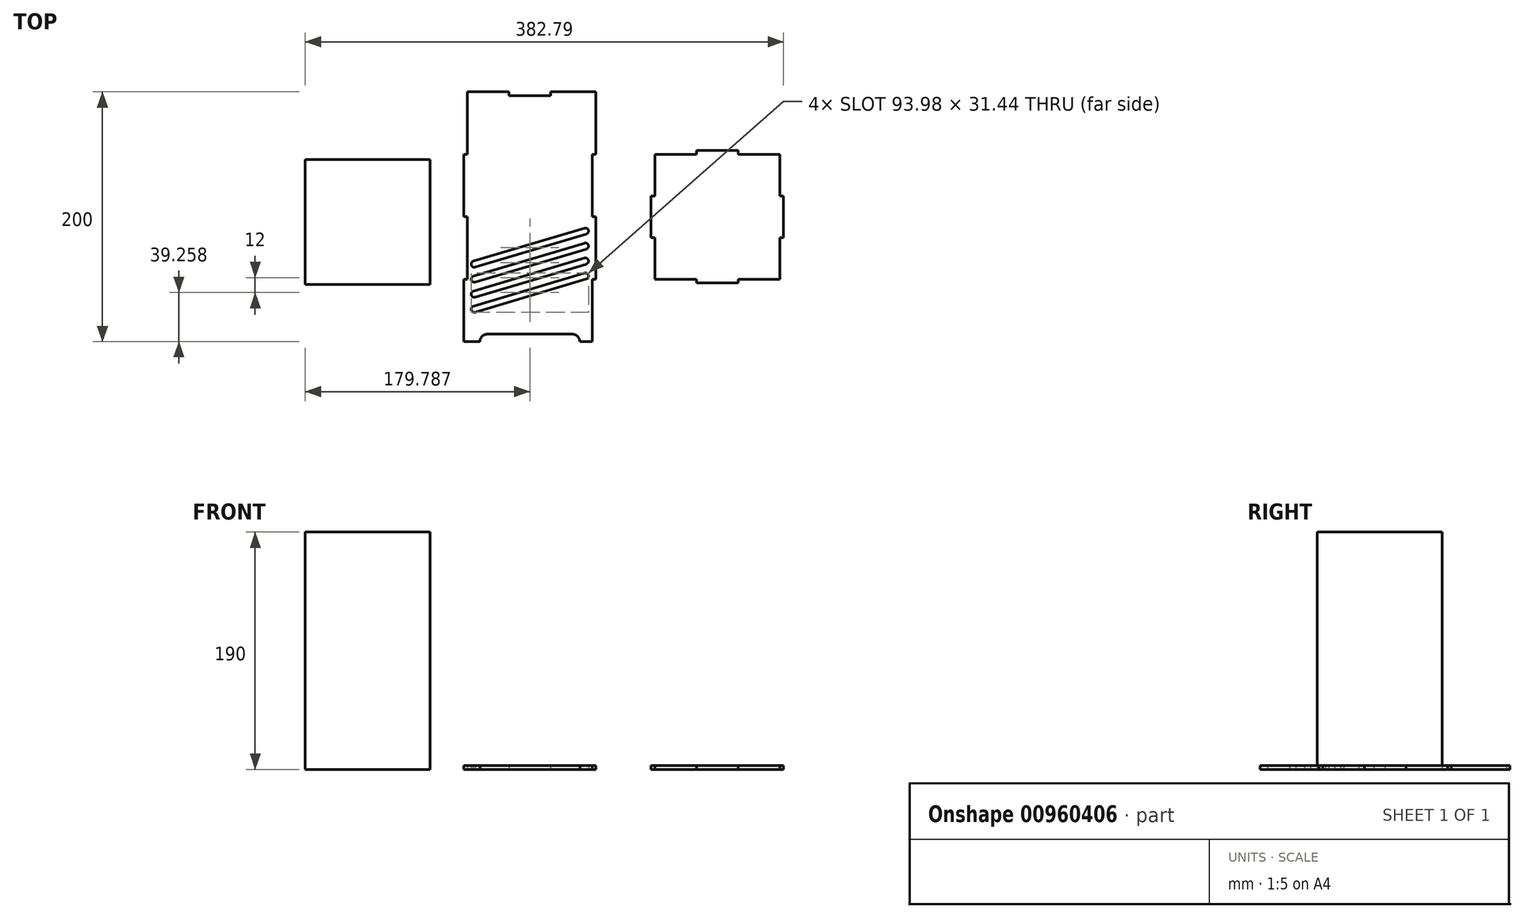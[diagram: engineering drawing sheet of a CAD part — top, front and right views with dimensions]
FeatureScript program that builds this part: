
annotation { "Feature Type Name" : "Feature", "Feature Type Description" : "" }
export const myFeature = defineFeature(function(context is Context, id is Id, definition is map)
    precondition{}
    {
        {
            var Q0;
            Q0=qCreatedBy(makeId("Top.planeOp"),FACE);
            var sketch = newSketch(context, id + "F0", { "sketchPlane" : qUnion([Q0])});
            skLineSegment(sketch, "E0.bottom", {"start": v(50, 100) * mm, "end": v(-50, 100) * mm, "construction": true});
            skLineSegment(sketch, "E0.top", {"start": v(50, -100) * mm, "end": v(-50, -100) * mm, "construction": true});
            skLineSegment(sketch, "E0.left", {"start": v(50, 100) * mm, "end": v(50, -100) * mm, "construction": true});
            skLineSegment(sketch, "E0.right", {"start": v(-50, 100) * mm, "end": v(-50, -100) * mm, "construction": true});
            skLineSegment(sketch, "E1", {"start": v(-50, 100) * mm, "end": v(-50, 50) * mm});
            skLineSegment(sketch, "E2", {"start": v(-50, 50) * mm, "end": v(-53, 50) * mm});
            skLineSegment(sketch, "E3", {"start": v(-53, 50) * mm, "end": v(-53, 0) * mm});
            skLineSegment(sketch, "E4", {"start": v(-53, 0) * mm, "end": v(-50, 0) * mm});
            skLineSegment(sketch, "E5", {"start": v(-50, 0) * mm, "end": v(-50, -50) * mm});
            skLineSegment(sketch, "E6", {"start": v(-50, -50) * mm, "end": v(-53, -50) * mm});
            skLineSegment(sketch, "E7", {"start": v(-53, -50) * mm, "end": v(-53, -100) * mm});
            skLineSegment(sketch, "E8", {"start": v(-53, -100) * mm, "end": v(-50, -100) * mm});
            skLineSegment(sketch, "E9", {"start": v(50, 100) * mm, "end": v(53, 100) * mm});
            skLineSegment(sketch, "E10", {"start": v(53, 100) * mm, "end": v(53, 50) * mm});
            skLineSegment(sketch, "E11", {"start": v(53, 50) * mm, "end": v(50, 50) * mm});
            skLineSegment(sketch, "E12", {"start": v(50, 50) * mm, "end": v(50, 0) * mm});
            skLineSegment(sketch, "E13", {"start": v(50, 0) * mm, "end": v(53, 0) * mm});
            skLineSegment(sketch, "E14", {"start": v(53, 0) * mm, "end": v(53, -50) * mm});
            skLineSegment(sketch, "E15", {"start": v(53, -50) * mm, "end": v(50, -50) * mm});
            skLineSegment(sketch, "E16", {"start": v(50, -50) * mm, "end": v(50, -100) * mm});
            skLineSegment(sketch, "E17", {"start": v(50, -100) * mm, "end": v(-50, -100) * mm});
            skLineSegment(sketch, "E18.bottom", {"start": v(100, -50) * mm, "end": v(200, -50) * mm, "construction": true});
            skLineSegment(sketch, "E18.top", {"start": v(100, 50) * mm, "end": v(200, 50) * mm, "construction": true});
            skLineSegment(sketch, "E18.left", {"start": v(100, -50) * mm, "end": v(100, 50) * mm, "construction": true});
            skLineSegment(sketch, "E18.right", {"start": v(200, -50) * mm, "end": v(200, 50) * mm, "construction": true});
            skPoint(sketch, "E18.middle", {"position": v(150, 0) * mm});
            skLineSegment(sketch, "E19", {"start": v(100, 50) * mm, "end": v(133.33, 50) * mm});
            skLineSegment(sketch, "E20", {"start": v(133.33, 50) * mm, "end": v(133.33, 53) * mm});
            skLineSegment(sketch, "E21", {"start": v(133.33, 53) * mm, "end": v(166.67, 53) * mm});
            skLineSegment(sketch, "E22", {"start": v(166.67, 53) * mm, "end": v(166.67, 50) * mm});
            skLineSegment(sketch, "E23", {"start": v(166.67, 50) * mm, "end": v(200, 50) * mm});
            skLineSegment(sketch, "E24", {"start": v(-50, 100) * mm, "end": v(-16.67, 100) * mm});
            skLineSegment(sketch, "E25", {"start": v(-16.67, 97) * mm, "end": v(-16.67, 100) * mm});
            skLineSegment(sketch, "E26", {"start": v(-16.67, 97) * mm, "end": v(16.67, 97) * mm});
            skLineSegment(sketch, "E27", {"start": v(16.67, 100) * mm, "end": v(16.67, 97) * mm});
            skLineSegment(sketch, "E28", {"start": v(16.67, 100) * mm, "end": v(50, 100) * mm});
            skLineSegment(sketch, "E29.1.1", {"start": v(97, -16.67) * mm, "end": v(97, 16.67) * mm});
            skLineSegment(sketch, "E29.1.2", {"start": v(100, -50) * mm, "end": v(100, -16.67) * mm});
            skLineSegment(sketch, "E29.1.3", {"start": v(100, 16.67) * mm, "end": v(100, 50) * mm});
            skLineSegment(sketch, "E29.1.4", {"start": v(100, -16.67) * mm, "end": v(97, -16.67) * mm});
            skLineSegment(sketch, "E29.1.5", {"start": v(97, 16.67) * mm, "end": v(100, 16.67) * mm});
            skLineSegment(sketch, "E29.2.0", {"start": v(200, -50) * mm, "end": v(100, -50) * mm, "construction": true});
            skLineSegment(sketch, "E29.2.1", {"start": v(166.67, -53) * mm, "end": v(133.33, -53) * mm});
            skLineSegment(sketch, "E29.2.2", {"start": v(200, -50) * mm, "end": v(166.67, -50) * mm});
            skLineSegment(sketch, "E29.2.3", {"start": v(133.33, -50) * mm, "end": v(100, -50) * mm});
            skLineSegment(sketch, "E29.2.4", {"start": v(166.67, -50) * mm, "end": v(166.67, -53) * mm});
            skLineSegment(sketch, "E29.2.5", {"start": v(133.33, -53) * mm, "end": v(133.33, -50) * mm});
            skLineSegment(sketch, "E29.3.0", {"start": v(200, 50) * mm, "end": v(200, -50) * mm, "construction": true});
            skLineSegment(sketch, "E29.3.1", {"start": v(203, 16.67) * mm, "end": v(203, -16.67) * mm});
            skLineSegment(sketch, "E29.3.2", {"start": v(200, 50) * mm, "end": v(200, 16.67) * mm});
            skLineSegment(sketch, "E29.3.3", {"start": v(200, -16.67) * mm, "end": v(200, -50) * mm});
            skLineSegment(sketch, "E29.3.4", {"start": v(200, 16.67) * mm, "end": v(203, 16.67) * mm});
            skLineSegment(sketch, "E29.3.5", {"start": v(203, -16.67) * mm, "end": v(200, -16.67) * mm});
            skLineSegment(sketch, "E30.bottom", {"start": v(-47, 94) * mm, "end": v(47, 94) * mm, "construction": true});
            skLineSegment(sketch, "E30.left", {"start": v(-47, 94) * mm, "end": v(-47, -90) * mm, "construction": true});
            skLineSegment(sketch, "E30.right", {"start": v(47, 94) * mm, "end": v(47, -90) * mm, "construction": true});
            skPoint(sketch, "E31", {"position": v(0, 94) * mm});
            skArc(sketch, "E32", {"start": v(40, -100) * mm, "mid": v(38.24, -95.76) * mm, "end": v(34, -94) * mm});
            skArc(sketch, "E33", {"start": v(-40, -100) * mm, "mid": v(-38.24, -95.76) * mm, "end": v(-34, -94) * mm});
            skLineSegment(sketch, "E34", {"start": v(-34, -94) * mm, "end": v(34, -94) * mm});
            skLineSegment(sketch, "E35", {"start": v(-47, -90) * mm, "end": v(47, -90) * mm, "construction": true});
            skLineSegment(sketch, "E36", {"start": v(-45.28, -71.6) * mm, "end": v(43.79, -45.11) * mm});
            skLineSegment(sketch, "E37", {"start": v(43.79, -45.11) * mm, "end": v(45.21, -49.9) * mm, "construction": true});
            skLineSegment(sketch, "E38", {"start": v(45.21, -49.9) * mm, "end": v(-43.72, -76.35) * mm});
            skLineSegment(sketch, "E39", {"start": v(-43.72, -76.35) * mm, "end": v(-45.28, -71.6) * mm, "construction": true});
            skPoint(sketch, "E40", {"position": v(-44.5, -73.97) * mm});
            skPoint(sketch, "E41", {"position": v(44.5, -47.5) * mm});
            skArc(sketch, "E42", {"start": v(-43.72, -76.35) * mm, "mid": v(-46.88, -74.75) * mm, "end": v(-45.28, -71.6) * mm});
            skArc(sketch, "E43", {"start": v(45.21, -49.9) * mm, "mid": v(46.9, -46.8) * mm, "end": v(43.79, -45.11) * mm});
            skArc(sketch, "E44.0.1.0", {"start": v(-43.72, -64.35) * mm, "mid": v(-46.88, -62.75) * mm, "end": v(-45.28, -59.6) * mm});
            skLineSegment(sketch, "E44.0.1.1", {"start": v(45.21, -37.9) * mm, "end": v(-43.72, -64.35) * mm});
            skLineSegment(sketch, "E44.0.1.2", {"start": v(-45.28, -59.6) * mm, "end": v(43.79, -33.11) * mm});
            skArc(sketch, "E44.0.1.3", {"start": v(45.21, -37.9) * mm, "mid": v(46.9, -34.8) * mm, "end": v(43.79, -33.11) * mm});
            skArc(sketch, "E44.0.2.0", {"start": v(-43.72, -52.35) * mm, "mid": v(-46.88, -50.75) * mm, "end": v(-45.28, -47.6) * mm});
            skLineSegment(sketch, "E44.0.2.1", {"start": v(45.21, -25.9) * mm, "end": v(-43.72, -52.35) * mm});
            skLineSegment(sketch, "E44.0.2.2", {"start": v(-45.28, -47.6) * mm, "end": v(43.79, -21.11) * mm});
            skArc(sketch, "E44.0.2.3", {"start": v(45.21, -25.9) * mm, "mid": v(46.9, -22.8) * mm, "end": v(43.79, -21.11) * mm});
            skArc(sketch, "E44.0.3.0", {"start": v(-43.72, -40.35) * mm, "mid": v(-46.88, -38.75) * mm, "end": v(-45.28, -35.6) * mm});
            skLineSegment(sketch, "E44.0.3.1", {"start": v(45.21, -13.9) * mm, "end": v(-43.72, -40.35) * mm});
            skLineSegment(sketch, "E44.0.3.2", {"start": v(-45.28, -35.6) * mm, "end": v(43.79, -9.11) * mm});
            skArc(sketch, "E44.0.3.3", {"start": v(45.21, -13.9) * mm, "mid": v(46.9, -10.8) * mm, "end": v(43.79, -9.11) * mm});
            skLineSegment(sketch, "E44.direction1", {"start": v(-43.72, -76.35) * mm, "end": v(-18.72, -76.35) * mm, "construction": true});
            skLineSegment(sketch, "E44.direction2", {"start": v(-43.72, -76.35) * mm, "end": v(-43.72, -64.35) * mm, "construction": true});
            skSolve(sketch);
        }
        {
            var Q0;
            {var subQ1=sQuery(id+"F0.wireOp",EDGE,"E1");Q0=makeQuery(id+"F0.imprint","IMPRINT",FACE,{"disambiguationData":[TD([[makeQuery(id+"F0.imprint","IMPRINT",EDGE,{"derivedFrom":subQ1}),1.0]])]});}
            var Q1;
            Q1=makeQuery(id+"F0.imprint","IMPRINT",FACE,{"disambiguationData":[TD([[makeQuery(id+"F0.imprint","IMPRINT",EDGE,{"derivedFrom":sQuery(id+"F0.wireOp",EDGE,"E19")}),-1.0]])]});
            var Q2;
            Q2=makeQuery(id+"F0.imprint","IMPRINT",FACE,{"disambiguationData":[TD([[makeQuery(id+"F0.imprint","IMPRINT",EDGE,{"derivedFrom":sQuery(id+"F0.wireOp",EDGE,"Keu7CFB7-OzkV-kheK-EioE-kCD04RJ6AMgD")}),-1.0]])]});
            var Q3;
            Q3=makeQuery(id+"F0.imprint","IMPRINT",FACE,{"disambiguationData":[TD([[makeQuery(id+"F0.imprint","IMPRINT",EDGE,{"derivedFrom":sQuery(id+"F0.wireOp",EDGE,"CxqOxMkw-QS5D-0mn4-owi1-HJOZ3keFKIxb")}),-1.0]])]});
            var Q4;
            {var subQ0=sQuery(id+"F0.wireOp",EDGE,"G1pd2ycF-LF3J-OOJV-xg43-P0z7lfAEKcbT");Q4=makeQuery(id+"F0.imprint","IMPRINT",FACE,{"disambiguationData":[TD([[makeQuery(id+"F0.imprint","IMPRINT",EDGE,{"derivedFrom":subQ0}),1.0]])]});}
            var Q5;
            {var subQ0=sQuery(id+"F0.wireOp",EDGE,"3pNC7KNG-2ofq-2Sgq-uzQG-ekGvzRAEndBU");Q5=makeQuery(id+"F0.imprint","IMPRINT",FACE,{"disambiguationData":[TD([[makeQuery(id+"F0.imprint","IMPRINT",EDGE,{"derivedFrom":subQ0}),1.0]])]});}
            var Q6;
            {var subQ0=sQuery(id+"F0.wireOp",EDGE,"LXJbpEfZ-frzx-Y1Sh-Le5r-K20tUTRIz8wG");Q6=makeQuery(id+"F0.imprint","IMPRINT",FACE,{"disambiguationData":[TD([[makeQuery(id+"F0.imprint","IMPRINT",EDGE,{"derivedFrom":subQ0}),1.0]])]});}
            var Q7;
            {var subQ0=sQuery(id+"F0.wireOp",EDGE,"xlwis0tu-sNfi-IORW-EiwS-mWuVUJjCJIh6");Q7=makeQuery(id+"F0.imprint","IMPRINT",FACE,{"disambiguationData":[TD([[makeQuery(id+"F0.imprint","IMPRINT",EDGE,{"derivedFrom":subQ0}),1.0]])]});}
            var Q8;
            {var subQ1=sQuery(id+"F0.wireOp",EDGE,"eXAwmtIw-vpKg-XvSc-I5D1-JsT2yTh656DQ");Q8=makeQuery(id+"F0.imprint","IMPRINT",FACE,{"disambiguationData":[TD([[makeQuery(id+"F0.imprint","IMPRINT",EDGE,{"derivedFrom":subQ1}),1.0]])]});}
            var Q9;
            {var subQ2=sQuery(id+"F0.wireOp",EDGE,"qABGjfcH-giEb-9wEi-zCJ1-TrGhvMvMYIv7");Q9=makeQuery(id+"F0.imprint","IMPRINT",FACE,{"disambiguationData":[TD([[makeQuery(id+"F0.imprint","IMPRINT",EDGE,{"derivedFrom":subQ2}),1.0]])]});}
            var Q10;
            {var subQ0=sQuery(id+"F0.wireOp",EDGE,"Rn0nwcxM-LJV5-V64v-ZTzT-QAsZKO2SUoVm");Q10=makeQuery(id+"F0.imprint","IMPRINT",FACE,{"disambiguationData":[TD([[makeQuery(id+"F0.imprint","IMPRINT",EDGE,{"derivedFrom":subQ0}),-1.0]])]});}
            extrude(context, id + "F1", {"entities" : qUnion([Q0, Q1, Q2, Q3, Q4, Q5, Q6, Q7, Q8, Q9, Q10]), "depth" : 3 * mm, "offsetDistance" : 25 * mm});
        }
        {
            var Q0;
            Q0=qCreatedBy(makeId("Top.planeOp"),FACE);
            var sketch = newSketch(context, id + "F2", { "sketchPlane" : qUnion([Q0])});
            skLineSegment(sketch, "E45.bottom", {"start": v(-79.79, 45.67) * mm, "end": v(-179.79, 45.67) * mm});
            skLineSegment(sketch, "E45.top", {"start": v(-79.79, -54.33) * mm, "end": v(-179.79, -54.33) * mm});
            skLineSegment(sketch, "E45.left", {"start": v(-79.79, 45.67) * mm, "end": v(-79.79, -54.33) * mm});
            skLineSegment(sketch, "E45.right", {"start": v(-179.79, 45.67) * mm, "end": v(-179.79, -54.33) * mm});
            skSolve(sketch);
        }
        {
            var Q0;
            Q0=qSketchRegion(id+"F2",true);
            extrude(context, id + "F3", {"entities" : qUnion([Q0]), "depth" : 190 * mm, "offsetDistance" : 25 * mm});
        }
    });
